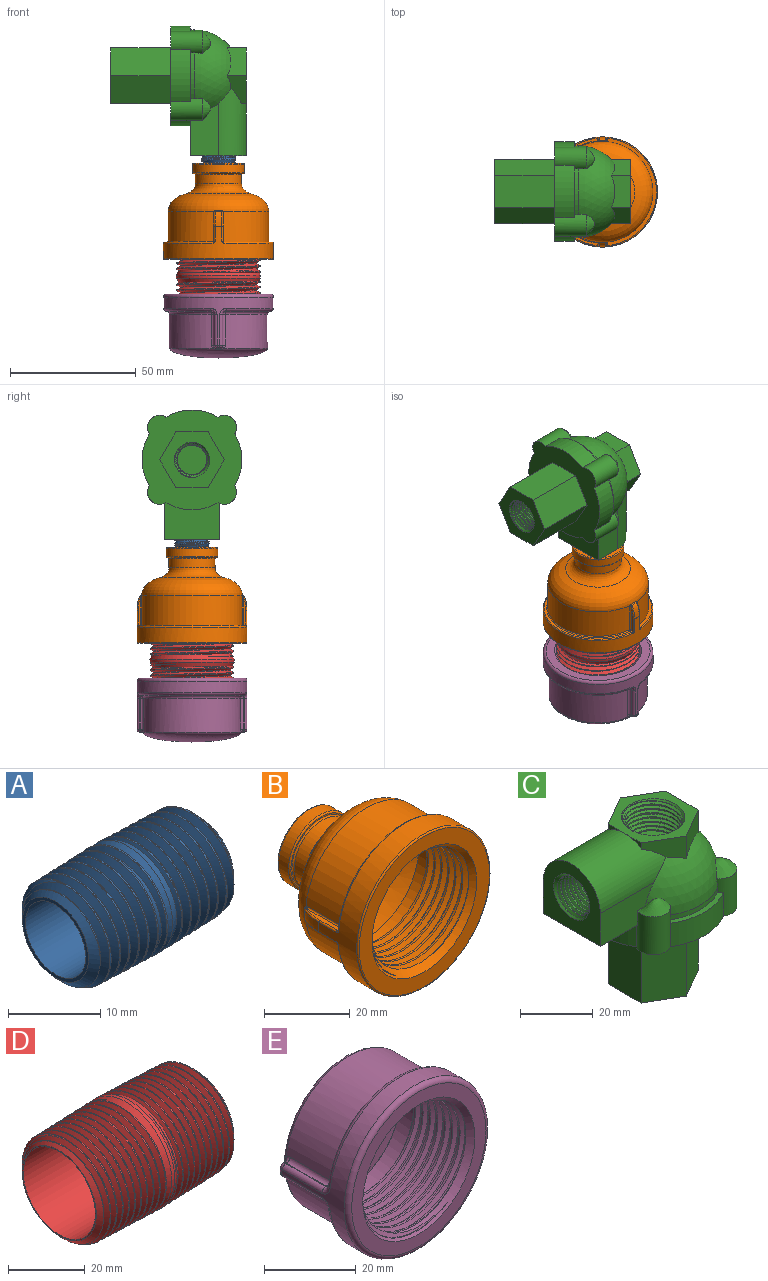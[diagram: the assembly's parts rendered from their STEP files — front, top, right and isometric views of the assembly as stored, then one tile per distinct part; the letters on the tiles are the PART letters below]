
ASSEMBLY  parts=5 mates=9
PART A: 109 faces, bbox 22.5x14.3x14.3 mm
  f0: plane 10.13x10.13mm, normal (-1,0,0), area 13.5mm2, adj f1,f108
  f1: cylinder r=4.62mm len=22.23mm, axis (1,0,0), area 645.5mm2, adj f0,f2
  f2: plane 10.13x10.13mm, normal (1,0,0), area 13.5mm2, adj f1,f3
  f3: cone r=5.07mm half-angle=46.8deg, axis (-1,0,0), area 44.8mm2, adj f2,f4,f106,f107
  f4: bspline ~12.19x12.15mm, area 38.6mm2, adj f3,f5,f105,f106
  f5: bspline ~13.46x13.4mm, area 266.1mm2, adj f4,f6,f7,f8,f9,f10,f11,f12
  f6: bspline ~3.82x0.92mm, area 0mm2, adj f5,f19,f107
  f7: bspline ~4.28x3.3mm, area 0mm2, adj f5,f19
  f8: bspline ~5.31x1.19mm, area 0mm2, adj f5,f19
  f9: bspline ~4.66x2.76mm, area 0mm2, adj f5,f19
  f10: bspline ~5.15x1.7mm, area 0mm2, adj f5,f19
  f11: bspline ~5.56x2.66mm, area 0mm2, adj f5,f19
  f12: bspline ~5.66x2.45mm, area 0mm2, adj f5,f19
  f13: bspline ~4.61x2.88mm, area 0mm2, adj f5,f19
  f14: bspline ~4.92x3.74mm, area 0mm2, adj f5,f19
  f15: bspline ~6.53x1.24mm, area 0mm2, adj f5,f19
  f16: bspline ~3.92x3.79mm, area 0mm2, adj f5,f19
  f17: bspline ~6.52x1.39mm, area 0mm2, adj f5,f19
  f18: bspline ~5.36x1.25mm, area 0mm2, adj f5,f19
  f19: cone r=6.86mm half-angle=1.8deg, axis (-1,0,0), area 71.4mm2, adj f5,f6,f7,f8,f9,f10,f11,f12
  f20: bspline ~6.23x2.37mm, area 0mm2, adj f5,f19
  f21: bspline ~6.05x2.65mm, area 0mm2, adj f5,f19
  f22: bspline ~4.95x2.37mm, area 0mm2, adj f5,f19
  f23: bspline ~5.28x1.57mm, area 0mm2, adj f5,f19
  f24: bspline ~5.15x3.53mm, area 0mm2, adj f5,f19
  f25: bspline ~5.44x1.08mm, area 0mm2, adj f5,f19
  f26: bspline ~5.08x4.22mm, area 0mm2, adj f5,f19
  f27: bspline ~6.25x1mm, area 0mm2, adj f5,f19
  f28: bspline ~4.82x4.54mm, area 0mm2, adj f5,f19
  f29: bspline ~5.5x0.86mm, area 0mm2, adj f5,f19
  f30: bspline ~4.46x3.27mm, area 0mm2, adj f5,f19
  f31: bspline ~5.41x1.32mm, area 0mm2, adj f5,f19
  f32: bspline ~5.79x3.25mm, area 0mm2, adj f5,f19
  f33: bspline ~5.99x2.15mm, area 0mm2, adj f5,f19
  f34: bspline ~5.14x2.1mm, area 0mm2, adj f5,f19
  f35: bspline ~5.97x2.97mm, area 0mm2, adj f5,f19
  f36: bspline ~6.03x2.18mm, area 0mm2, adj f5,f19
  f37: bspline ~4.65x3.06mm, area 0mm2, adj f5,f19
  f38: bspline ~5.51x1.05mm, area 0mm2, adj f5,f19
  f39: bspline ~4.24x3.61mm, area 0mm2, adj f5,f19
  f40: bspline ~6.68x1.16mm, area 0mm2, adj f5,f19
  f41: bspline ~4.11x3.78mm, area 0mm2, adj f5,f19
  f42: bspline ~6.32x1.29mm, area 0mm2, adj f5,f19
  f43: bspline ~4.55x3.25mm, area 0mm2, adj f5,f19
  f44: bspline ~5.45x1.38mm, area 0mm2, adj f5,f19
  f45: bspline ~4.92x2.68mm, area 0mm2, adj f5,f19
  f46: bspline ~6.31x2.52mm, area 0mm2, adj f5,f19
  f47: bspline ~5.58x2.31mm, area 0mm2, adj f5,f19
  f48: bspline ~5x2.55mm, area 0mm2, adj f5,f19
  f49: bspline ~5.44x1.5mm, area 0mm2, adj f5,f19
  f50: bspline ~4.98x2.91mm, area 0mm2, adj f5,f19,f51
  f51: cone r=6.52mm half-angle=45deg, axis (1,0,0), area 2.8mm2, adj f5,f19,f50,f52,f106
  f52: cone r=6.86mm half-angle=25deg, axis (-1,0,0), area 44.7mm2, adj f5,f51,f53,f105,f106
  f53: cone r=6.86mm half-angle=25deg, axis (1,0,0), area 43.3mm2, adj f52,f54,f56,f103,f104
  f54: cone r=6.86mm half-angle=25deg, axis (1,0,0), area 7.1mm2, adj f53,f55,f56,f104
  f55: bspline ~12.19x12.15mm, area 38.6mm2, adj f54,f56,f104,f108
  f56: bspline ~13.46x13.4mm, area 266.1mm2, adj f53,f54,f55,f57,f58,f59,f60,f61
  f57: cone r=5.07mm half-angle=46.8deg, axis (1,0,0), area 5.9mm2, adj f56,f58,f71,f104,f108
  f58: bspline ~3.82x0.92mm, area 0mm2, adj f56,f57,f71
  f59: bspline ~4.28x3.3mm, area 0mm2, adj f56,f71
  f60: bspline ~5.31x1.19mm, area 0mm2, adj f56,f71
  f61: bspline ~4.66x2.76mm, area 0mm2, adj f56,f71
  f62: bspline ~5.15x1.7mm, area 0mm2, adj f56,f71
  f63: bspline ~5.56x2.66mm, area 0mm2, adj f56,f71
  f64: bspline ~5.66x2.45mm, area 0mm2, adj f56,f71
  f65: bspline ~4.61x2.88mm, area 0mm2, adj f56,f71
  f66: bspline ~4.92x3.74mm, area 0mm2, adj f56,f71
  f67: bspline ~6.53x1.24mm, area 0mm2, adj f56,f71
  f68: bspline ~3.92x3.79mm, area 0mm2, adj f56,f71
  f69: bspline ~6.52x1.39mm, area 0mm2, adj f56,f71
  f70: bspline ~5.36x1.25mm, area 0mm2, adj f56,f71
  f71: cone r=6.86mm half-angle=1.8deg, axis (1,0,0), area 71.4mm2, adj f56,f57,f58,f59,f60,f61,f62,f63
  f72: bspline ~6.23x2.37mm, area 0mm2, adj f56,f71
  f73: bspline ~6.05x2.65mm, area 0mm2, adj f56,f71
  f74: bspline ~4.95x2.37mm, area 0mm2, adj f56,f71
  f75: bspline ~5.28x1.57mm, area 0mm2, adj f56,f71
  f76: bspline ~5.15x3.53mm, area 0mm2, adj f56,f71
  f77: bspline ~5.44x1.08mm, area 0mm2, adj f56,f71
  f78: bspline ~5.08x4.22mm, area 0mm2, adj f56,f71
  f79: bspline ~6.25x1mm, area 0mm2, adj f56,f71
  f80: bspline ~4.82x4.54mm, area 0mm2, adj f56,f71
  f81: bspline ~5.5x0.86mm, area 0mm2, adj f56,f71
  f82: bspline ~4.46x3.27mm, area 0mm2, adj f56,f71
  f83: bspline ~5.41x1.32mm, area 0mm2, adj f56,f71
  f84: bspline ~5.79x3.25mm, area 0mm2, adj f56,f71
  f85: bspline ~5.99x2.15mm, area 0mm2, adj f56,f71
  f86: bspline ~5.14x2.1mm, area 0mm2, adj f56,f71
  f87: bspline ~5.97x2.97mm, area 0mm2, adj f56,f71
  f88: bspline ~6.03x2.18mm, area 0mm2, adj f56,f71
  f89: bspline ~4.65x3.06mm, area 0mm2, adj f56,f71
  f90: bspline ~5.51x1.05mm, area 0mm2, adj f56,f71
  f91: bspline ~4.24x3.61mm, area 0mm2, adj f56,f71
  f92: bspline ~6.68x1.16mm, area 0mm2, adj f56,f71
  f93: bspline ~4.11x3.78mm, area 0mm2, adj f56,f71
  f94: bspline ~6.32x1.29mm, area 0mm2, adj f56,f71
  f95: bspline ~4.55x3.25mm, area 0mm2, adj f56,f71
  f96: bspline ~5.45x1.38mm, area 0mm2, adj f56,f71
  f97: bspline ~4.92x2.68mm, area 0mm2, adj f56,f71
  f98: bspline ~6.31x2.52mm, area 0mm2, adj f56,f71
  f99: bspline ~5.58x2.31mm, area 0mm2, adj f56,f71
  f100: bspline ~5x2.55mm, area 0mm2, adj f56,f71
  f101: bspline ~5.44x1.5mm, area 0mm2, adj f56,f71
  f102: bspline ~4.98x2.91mm, area 0mm2, adj f56,f71,f103
  f103: cone r=6.52mm half-angle=45deg, axis (-1,0,0), area 2.8mm2, adj f53,f56,f71,f102,f104
  f104: bspline ~14.26x14.19mm, area 271.6mm2, adj f53,f54,f55,f57,f71,f103,f108
  f105: cone r=6.86mm half-angle=25deg, axis (-1,0,0), area 5.6mm2, adj f4,f5,f52,f106
  f106: bspline ~14.26x14.19mm, area 269.3mm2, adj f3,f4,f19,f51,f52,f105,f107
  f107: cone r=5.07mm half-angle=46.8deg, axis (-1,0,0), area 5.9mm2, adj f3,f5,f6,f19,f106
  f108: cone r=5.07mm half-angle=46.8deg, axis (1,0,0), area 44.8mm2, adj f0,f55,f57,f104
PART B: 72 faces, bbox 47.9x38.9x47.9 mm
  f0: cylinder r=21.84mm len=43.69mm, axis (0,-1,0), area 868.5mm2, adj f32,f33,f34,f36,f37,f39,f41,f49
  f1: plane 11.17x1.12mm, normal (0,0,-1), area 10.8mm2, adj f38,f40,f41,f43
  f2: plane 11.17x1.12mm, normal (0,0,1), area 10.8mm2, adj f50,f51,f57,f58
  f3: plane 11.17x1.12mm, normal (0,0,1), area 10.8mm2, adj f63,f67,f68,f69
  f4: plane 11.17x1.12mm, normal (0,0,-1), area 10.8mm2, adj f46,f48,f53,f56
  f5: cylinder r=7.11mm len=14.22mm, axis (0,1,0), area 217mm2, adj f29,f35
  f6: cylinder r=20mm len=39.82mm, axis (0,-1,0), area 692.4mm2, adj f18,f55,f58,f62,f63,f64
  f7: cylinder r=20mm len=39.82mm, axis (0,-1,0), area 715.6mm2, adj f9,f18,f38,f40,f42,f46,f48,f52
  f8: plane 42.69x19.34mm, normal (0,1,0), area 64.4mm2, adj f33,f57,f62,f68
  f9: plane 42.69x19.34mm, normal (0,1,0), area 87.9mm2, adj f7,f32,f38,f46
  f10: plane 42.89x42.89mm, normal (0,-1,0), area 510mm2, adj f11,f34
  f11: cone r=17.25mm half-angle=45deg, axis (0,-1,0), area 182mm2, adj f10,f12,f13,f14,f15
  f12: bspline ~33.55x33.52mm, area 845.3mm2, adj f11,f13,f15,f16
  f13: bspline ~30.92x30.89mm, area 310.9mm2, adj f11,f12,f14,f16
  f14: bspline ~33.57x33.54mm, area 804.5mm2, adj f11,f13,f15,f16
  f15: cone r=16.7mm half-angle=1.8deg, axis (0,-1,0), area 205.5mm2, adj f11,f12,f14,f16
  f16: plane 34.99x34.99mm, normal (0,1,0), area 165.6mm2, adj f12,f13,f14,f15,f17
  f17: cylinder r=17.21mm len=34.42mm, axis (0,-1,0), area 466.9mm2, adj f16,f35
  f18: revolved ~40.01x40.01mm, area 1167.6mm2, adj f6,f7,f19,f44,f45,f47,f59,f61
  f19: revolved ~25.71x25.71mm, area 382.1mm2, adj f18,f20
  f20: cylinder r=9.14mm len=18.29mm, axis (0,1,0), area 211.4mm2, adj f19,f71
  f21: plane 19.78x19.78mm, normal (0,-1,0), area 21.3mm2, adj f31,f71
  f22: cylinder r=10.29mm len=20.57mm, axis (0,1,0), area 211.4mm2, adj f30,f31
  f23: plane 19.78x19.78mm, normal (0,1,0), area 143.9mm2, adj f24,f30
  f24: cone r=7.21mm half-angle=45deg, axis (0,1,0), area 47.5mm2, adj f23,f25,f26,f27,f28
  f25: bspline ~12.22x12.15mm, area 65.6mm2, adj f24,f26,f27,f29
  f26: bspline ~13.91x13.83mm, area 184.1mm2, adj f24,f25,f28,f29
  f27: bspline ~13.89x13.88mm, area 175.3mm2, adj f24,f25,f28,f29
  f28: cone r=6.86mm half-angle=1.8deg, axis (0,1,0), area 46.6mm2, adj f24,f26,f27,f29
  f29: plane 14.65x14.65mm, normal (0,-1,0), area 38.2mm2, adj f5,f25,f26,f27,f28
  f30: torus R=9.89mm, axis (0,-1,0), area 39.7mm2, adj f22,f23
  f31: torus R=9.89mm, axis (0,1,0), area 39.7mm2, adj f21,f22
  f32: torus R=21.45mm, axis (0,-1,0), area 39.8mm2, adj f0,f9,f39,f49
  f33: torus R=21.45mm, axis (0,-1,0), area 39.8mm2, adj f0,f8,f54,f70
  f34: torus R=21.45mm, axis (0,-1,0), area 85mm2, adj f0,f10
  f35: cone r=0mm half-angle=59deg, axis (0,-1,0), area 900mm2, adj f5,f17
  f36: revolved ~6.05x2.87mm, area 17.5mm2, adj f0,f43,f45,f51
  f37: revolved ~6.05x2.87mm, area 17.3mm2, adj f0,f56,f61,f67
  f38: cylinder r=0.4mm len=1.52mm, axis (-1,0,0), area 0.8mm2, adj f1,f7,f9,f39,f40
  f39: bspline ~0.97x0.95mm, area 0.5mm2, adj f0,f32,f38,f41
  f40: cylinder r=0.4mm len=11.56mm, axis (0,-1,0), area 6.6mm2, adj f1,f7,f38,f42
  f41: cylinder r=0.4mm len=5.7mm, axis (0,-1,0), area 3.4mm2, adj f0,f1,f39,f43
  f42: bspline ~1.11x0.5mm, area 0.3mm2, adj f7,f40,f43,f44
  f43: bspline ~7.42x1.8mm, area 3.7mm2, adj f1,f36,f41,f42,f44
  f44: bspline ~0.79x0.55mm, area 0.2mm2, adj f18,f42,f43,f45
  f45: torus R=20.39mm, axis (0,-1,0), area 1.2mm2, adj f18,f36,f44,f47
  f46: cylinder r=0.4mm len=1.52mm, axis (-1,0,0), area 0.8mm2, adj f4,f7,f9,f48,f49
  f47: bspline ~0.79x0.55mm, area 0.2mm2, adj f18,f45,f51,f55
  f48: cylinder r=0.4mm len=11.56mm, axis (0,-1,0), area 6.6mm2, adj f4,f7,f46,f52
  f49: bspline ~0.99x0.89mm, area 0.5mm2, adj f0,f32,f46,f53
  f50: cylinder r=0.4mm len=5.7mm, axis (0,-1,0), area 3.4mm2, adj f0,f2,f51,f54
  f51: bspline ~7.42x1.8mm, area 3.7mm2, adj f2,f36,f47,f50,f55
  f52: bspline ~1.11x0.5mm, area 0.3mm2, adj f7,f48,f56,f59
  f53: cylinder r=0.4mm len=5.7mm, axis (0,-1,0), area 3.4mm2, adj f0,f4,f49,f56
  f54: bspline ~0.99x0.89mm, area 0.5mm2, adj f0,f33,f50,f57
  f55: bspline ~1.11x0.5mm, area 0.3mm2, adj f6,f47,f51,f58
  f56: bspline ~7.42x1.8mm, area 3.7mm2, adj f4,f37,f52,f53,f59
  f57: cylinder r=0.4mm len=1.12mm, axis (1,0,0), area 0.7mm2, adj f2,f8,f54,f60
  f58: cylinder r=0.4mm len=11.17mm, axis (0,-1,0), area 6.5mm2, adj f2,f6,f55,f60
  f59: bspline ~0.79x0.55mm, area 0.2mm2, adj f18,f52,f56,f61
  f60: sphere r=0.4mm, area 0.3mm2, adj f57,f58,f62
  f61: torus R=20.39mm, axis (0,-1,0), area 1.2mm2, adj f18,f37,f59,f65
  f62: torus R=20.4mm, axis (0,-1,0), area 36.9mm2, adj f6,f8,f60,f66
  f63: cylinder r=0.4mm len=11.17mm, axis (0,-1,0), area 6.5mm2, adj f3,f6,f64,f66
  f64: bspline ~1.11x0.5mm, area 0.3mm2, adj f6,f63,f65,f67
  f65: bspline ~0.79x0.55mm, area 0.2mm2, adj f18,f61,f64,f67
  f66: sphere r=0.4mm, area 0.3mm2, adj f62,f63,f68
  f67: bspline ~7.42x1.8mm, area 3.7mm2, adj f3,f37,f64,f65,f69
  f68: cylinder r=0.4mm len=1.12mm, axis (1,0,0), area 0.7mm2, adj f3,f8,f66,f70
  f69: cylinder r=0.4mm len=5.7mm, axis (0,-1,0), area 3.4mm2, adj f0,f3,f67,f70
  f70: bspline ~0.97x0.95mm, area 0.5mm2, adj f0,f33,f68,f69
  f71: torus R=9.54mm, axis (0,1,0), area 36.4mm2, adj f20,f21
PART C: 58 faces, bbox 52.9x40.7x55.6 mm
  f0: plane 22.23x22.23mm, normal (-1,0,0), area 285.5mm2, adj f10,f11,f23,f29,f46
  f1: plane 25.66x22.23mm, normal (0,0,-1), area 272.3mm2, adj f14,f15,f16,f17,f18,f19,f40
  f2: plane 20.71x4.04mm, normal (0,0,1), area 32.3mm2, adj f4,f7,f33,f35
  f3: cylinder r=18.26mm len=18.26mm, axis (0,0,-1), area 30.4mm2, adj f6,f32,f35,f39
  f4: cylinder r=19.84mm len=20.71mm, axis (0,0,1), area 172.9mm2, adj f2,f13,f33,f35
  f5: cylinder r=19.84mm len=20.71mm, axis (0,0,1), area 172.9mm2, adj f9,f13,f31,f33
  f6: plane 20.71x4.04mm, normal (0,0,1), area 32.3mm2, adj f3,f8,f32,f35
  f7: cylinder r=18.26mm len=18.26mm, axis (0,0,-1), area 30.4mm2, adj f2,f33,f35,f39
  f8: cylinder r=19.84mm len=20.71mm, axis (0,0,1), area 172.9mm2, adj f6,f13,f32,f35
  f9: plane 20.71x4.04mm, normal (0,0,1), area 32.3mm2, adj f5,f30,f31,f33
  f10: plane 21.55x11.82mm, normal (0,-1,0), area 188.7mm2, adj f0,f23,f29,f32,f38,f39
  f11: plane 21.55x11.82mm, normal (0,1,0), area 188.7mm2, adj f0,f23,f29,f31,f37,f39
  f12: cylinder r=19.84mm len=20.71mm, axis (0,0,1), area 172.9mm2, adj f13,f29,f31,f32
  f13: plane 39.69x39.69mm, normal (0,0,-1), area 899mm2, adj f4,f5,f8,f12,f14,f15,f16,f17
  f14: plane 23.81x11.11mm, normal (-0.5,0.87,0), area 305.6mm2, adj f1,f13,f15,f19
  f15: plane 23.81x12.83mm, normal (-1,0,0), area 305.6mm2, adj f1,f13,f14,f16
  f16: plane 23.81x11.11mm, normal (-0.5,-0.87,0), area 305.6mm2, adj f1,f13,f15,f17
  f17: plane 23.81x11.11mm, normal (0.5,-0.87,0), area 305.6mm2, adj f1,f13,f16,f18
  f18: plane 23.81x12.83mm, normal (1,0,0), area 305.6mm2, adj f1,f13,f17,f19
  f19: plane 23.81x11.11mm, normal (0.5,0.87,0), area 305.6mm2, adj f1,f13,f14,f18
  f20: plane 6.42x2.04mm, normal (-1,0,0), area 4.2mm2, adj f21,f23,f24
  f21: plane 25.66x22.23mm, normal (0,0,1), area 187.3mm2, adj f20,f22,f24,f25,f26,f27,f28,f52
  f22: plane 6.42x2.04mm, normal (-1,0,0), area 4.2mm2, adj f21,f23,f27
  f23: cylinder r=11.11mm len=26.76mm, axis (1,0,0), area 786.5mm2, adj f0,f10,f11,f20,f22,f24,f27,f39
  f24: plane 12x8.54mm, normal (-0.5,-0.87,0), area 65.1mm2, adj f20,f21,f23,f25,f39
  f25: plane 11.11x7.65mm, normal (0.5,-0.87,0), area 85.2mm2, adj f21,f24,f26,f39
  f26: plane 12.83x7.65mm, normal (1,0,0), area 85.2mm2, adj f21,f25,f28,f39
  f27: plane 12.11x8.65mm, normal (-0.5,0.87,0), area 65.1mm2, adj f21,f22,f23,f28,f39
  f28: plane 11.11x7.65mm, normal (0.5,0.87,0), area 85.2mm2, adj f21,f26,f27,f39
  f29: plane 22.23x14.82mm, normal (0,0,-1), area 288.2mm2, adj f0,f10,f11,f12,f31,f32
  f30: cylinder r=18.26mm len=18.26mm, axis (0,0,-1), area 30.4mm2, adj f9,f31,f33,f39
  f31: cylinder r=4.76mm len=12.7mm, axis (0,0,-1), area 167.8mm2, adj f5,f9,f11,f12,f13,f29,f30,f37
  f32: cylinder r=4.76mm len=12.7mm, axis (0,0,-1), area 167.8mm2, adj f3,f6,f8,f10,f12,f13,f29,f38
  f33: cylinder r=4.76mm len=12.7mm, axis (0,0,-1), area 180.3mm2, adj f2,f4,f5,f7,f9,f13,f30,f34
  f34: bspline ~9.75x9.43mm, area 57.4mm2, adj f33,f39
  f35: cylinder r=4.76mm len=12.7mm, axis (0,0,-1), area 180.3mm2, adj f2,f3,f4,f6,f7,f8,f13,f36
  f36: bspline ~9.75x9.44mm, area 57.1mm2, adj f35,f39
  f37: bspline ~9.44x6.76mm, area 52.3mm2, adj f11,f31,f39
  f38: bspline ~9.43x6.76mm, area 52.4mm2, adj f10,f32,f39
  f39: sphere r=18.26mm, area 1046.6mm2, adj f3,f7,f10,f11,f23,f24,f25,f26
  f40: cone r=7.03mm half-angle=45deg, axis (0,0,-1), area 36mm2, adj f1,f42,f43,f44,f45
  f41: plane 12.69x12.55mm, normal (0,0,-1), area 118.2mm2, adj f42,f43,f44,f45
  f42: bspline ~12.34x12.3mm, area 100.6mm2, adj f40,f41,f43,f44
  f43: bspline ~13.98x13.93mm, area 230.1mm2, adj f40,f41,f42,f45
  f44: bspline ~13.96x13.91mm, area 218.4mm2, adj f40,f41,f42,f45
  f45: cone r=6.86mm half-angle=1.8deg, axis (0,0,-1), area 52.8mm2, adj f40,f41,f43,f44
  f46: cone r=7.03mm half-angle=45deg, axis (-1,0,0), area 36mm2, adj f0,f48,f49,f50,f51
  f47: plane 12.69x12.55mm, normal (-1,0,0), area 118.2mm2, adj f48,f49,f50,f51
  f48: bspline ~12.34x12.3mm, area 100.6mm2, adj f46,f47,f49,f50
  f49: bspline ~13.98x13.93mm, area 230.1mm2, adj f46,f47,f48,f51
  f50: bspline ~13.96x13.91mm, area 218.4mm2, adj f46,f47,f48,f51
  f51: cone r=6.86mm half-angle=1.8deg, axis (-1,0,0), area 52.8mm2, adj f46,f47,f49,f50
  f52: cone r=8.75mm half-angle=45deg, axis (0,0,1), area 45.3mm2, adj f21,f54,f55,f56,f57
  f53: plane 16.12x15.95mm, normal (0,0,1), area 193.2mm2, adj f54,f55,f56,f57
  f54: bspline ~15.81x15.75mm, area 131.6mm2, adj f52,f53,f55,f56
  f55: bspline ~17.45x17.38mm, area 296.8mm2, adj f52,f53,f54,f57
  f56: bspline ~17.43x17.36mm, area 281.8mm2, adj f52,f53,f54,f57
  f57: cone r=8.57mm half-angle=1.8deg, axis (0,0,1), area 68.6mm2, adj f52,f53,f55,f56
PART D: 22 faces, bbox 50.9x33.4x33.4 mm
  f0: plane 27.33x27.33mm, normal (-1,0,0), area 28.9mm2, adj f6,f11
  f1: bspline ~33.44x33.4mm, area 1522.5mm2, adj f3,f4,f5,f6,f7,f9
  f2: bspline ~33.36x33.33mm, area 1586.2mm2, adj f3,f4,f5,f7,f8,f9
  f3: bspline ~30.4x30.36mm, area 243.4mm2, adj f1,f2,f6,f8,f9
  f4: cone r=15.87mm half-angle=45deg, axis (-1,0,0), area 15.3mm2, adj f1,f2,f5,f9
  f5: cone r=16.7mm half-angle=1.8deg, axis (1,0,0), area 262.8mm2, adj f1,f2,f4,f7
  f6: cone r=13.66mm half-angle=46.8deg, axis (1,0,0), area 183mm2, adj f0,f1,f3,f7
  f7: cone r=13.66mm half-angle=46.8deg, axis (1,0,0), area 22.5mm2, adj f1,f2,f5,f6
  f8: cone r=16.7mm half-angle=25deg, axis (1,0,0), area 0.8mm2, adj f2,f3,f9
  f9: cone r=16.7mm half-angle=25deg, axis (1,0,0), area 201mm2, adj f1,f2,f3,f4,f8,f10
  f10: cylinder r=16.7mm len=33.4mm, axis (-1,0,0), area 115.9mm2, adj f9,f21
  f11: cylinder r=13.32mm len=50.8mm, axis (1,0,0), area 4252.3mm2, adj f0,f12
  f12: plane 27.33x27.33mm, normal (1,0,0), area 28.9mm2, adj f11,f18
  f13: bspline ~33.44x33.4mm, area 1522.5mm2, adj f15,f16,f17,f18,f19,f21
  f14: bspline ~33.36x33.33mm, area 1586.2mm2, adj f15,f16,f17,f19,f20,f21
  f15: bspline ~30.4x30.36mm, area 243.4mm2, adj f13,f14,f18,f20,f21
  f16: cone r=15.87mm half-angle=45deg, axis (1,0,0), area 15.3mm2, adj f13,f14,f17,f21
  f17: cone r=16.7mm half-angle=1.8deg, axis (-1,0,0), area 262.8mm2, adj f13,f14,f16,f19
  f18: cone r=13.66mm half-angle=46.8deg, axis (-1,0,0), area 183mm2, adj f12,f13,f15,f19
  f19: cone r=13.66mm half-angle=46.8deg, axis (-1,0,0), area 22.5mm2, adj f13,f14,f17,f18
  f20: cone r=16.7mm half-angle=25deg, axis (-1,0,0), area 0.8mm2, adj f14,f15,f21
  f21: cone r=16.7mm half-angle=25deg, axis (-1,0,0), area 201mm2, adj f10,f13,f14,f15,f16,f20
PART E: 65 faces, bbox 47.4x25.5x47.4 mm
  f0: cylinder r=19.49mm len=38.69mm, axis (0,-1,0), area 750.4mm2, adj f20,f45,f49,f54,f58,f59
  f1: cylinder r=19.49mm len=38.69mm, axis (0,-1,0), area 750.4mm2, adj f20,f21,f25,f27,f34,f38
  f2: plane 41.34x41.34mm, normal (0,-1,0), area 407mm2, adj f4,f5
  f3: cylinder r=21.84mm len=43.69mm, axis (0,-1,0), area 657.2mm2, adj f4,f26,f31,f32,f37,f41,f42,f51
  f4: torus R=20.67mm, axis (0,-1,0), area 248.3mm2, adj f2,f3
  f5: cone r=17.25mm half-angle=45deg, axis (0,-1,0), area 154.5mm2, adj f2,f7,f8,f9,f10
  f6: plane 28.06x27.47mm, normal (0,-1,0), area 18.4mm2, adj f7,f9,f10,f16
  f7: bspline ~33.59x33.53mm, area 816.3mm2, adj f5,f6,f8,f10,f15
  f8: bspline ~31.47x31.41mm, area 384.4mm2, adj f5,f7,f9,f15
  f9: bspline ~33.6x33.57mm, area 773.5mm2, adj f5,f6,f8,f10,f15
  f10: cone r=16.7mm half-angle=1.8deg, axis (0,-1,0), area 458.2mm2, adj f5,f6,f7,f9
  f11: plane 12.27x0.2mm, normal (0,0,-1), area 2.4mm2, adj f33,f34,f42,f43
  f12: plane 12.27x0.2mm, normal (0,0,1), area 2.4mm2, adj f53,f58,f61,f64
  f13: plane 12.27x0.2mm, normal (0,0,1), area 2.4mm2, adj f40,f49,f50,f51
  f14: plane 12.27x0.2mm, normal (0,0,-1), area 2.4mm2, adj f21,f22,f30,f31
  f15: plane 26.78x26.15mm, normal (0,1,0), area 16.3mm2, adj f7,f8,f9,f16
  f16: cylinder r=15.68mm len=31.37mm, axis (0,-1,0), area 407.8mm2, adj f6,f15,f17
  f17: revolved ~31.37x15.68mm, area 0mm2, adj f16
  f18: plane 1.08x0.38mm, normal (0,1,0), area 0.4mm2, adj f43,f44,f52,f53
  f19: plane 1.08x0.38mm, normal (0,1,0), area 0.4mm2, adj f29,f30,f40,f41
  f20: revolved ~38.99x38.99mm, area 1302.5mm2, adj f0,f1,f24,f29,f35,f39,f44,f48
  f21: cylinder r=1.17mm len=12.27mm, axis (0,-1,0), area 20.6mm2, adj f1,f14,f23,f25
  f22: cylinder r=1.17mm len=1.17mm, axis (-1,0,0), area 0.2mm2, adj f14,f23,f26
  f23: sphere r=1.17mm, area 2mm2, adj f21,f22,f27
  f24: bspline ~2.47x1.21mm, area 2mm2, adj f20,f25,f29,f30
  f25: bspline ~1.98x1.31mm, area 1.4mm2, adj f1,f21,f24,f30
  f26: bspline ~2.75x2.63mm, area 4.7mm2, adj f3,f22,f31,f32
  f27: torus R=20.67mm, axis (0,-1,0), area 105.2mm2, adj f1,f23,f28,f32
  f28: sphere r=1.17mm, area 2mm2, adj f27,f33,f34
  f29: torus R=20.3mm, axis (0,-1,0), area 1.2mm2, adj f19,f20,f24,f35
  f30: cylinder r=1.17mm len=1.17mm, axis (1,0,0), area 0.4mm2, adj f14,f19,f24,f25,f36
  f31: cylinder r=1.17mm len=12.27mm, axis (0,-1,0), area 22.3mm2, adj f3,f14,f26,f36
  f32: torus R=20.67mm, axis (0,-1,0), area 113.1mm2, adj f3,f26,f27,f37
  f33: cylinder r=1.17mm len=1.17mm, axis (-1,0,0), area 0.2mm2, adj f11,f28,f37
  f34: cylinder r=1.17mm len=12.27mm, axis (0,-1,0), area 20.6mm2, adj f1,f11,f28,f38
  f35: bspline ~2.13x1.21mm, area 2mm2, adj f20,f29,f40,f45
  f36: sphere r=1.17mm, area 2.1mm2, adj f30,f31,f41
  f37: bspline ~2.89x2.88mm, area 4.7mm2, adj f3,f32,f33,f42
  f38: bspline ~1.98x1.31mm, area 1.4mm2, adj f1,f34,f39,f43
  f39: bspline ~2.13x1.21mm, area 2mm2, adj f20,f38,f43,f44
  f40: cylinder r=1.17mm len=1.17mm, axis (-1,0,0), area 0.4mm2, adj f13,f19,f35,f45,f46
  f41: torus R=20.67mm, axis (0,-1,0), area 2.1mm2, adj f3,f19,f36,f46
  f42: cylinder r=1.17mm len=12.27mm, axis (0,-1,0), area 22.3mm2, adj f3,f11,f37,f47
  f43: cylinder r=1.17mm len=1.17mm, axis (1,0,0), area 0.4mm2, adj f11,f18,f38,f39,f47
  f44: torus R=20.3mm, axis (0,-1,0), area 1.2mm2, adj f18,f20,f39,f48
  f45: bspline ~1.98x1.31mm, area 1.4mm2, adj f0,f35,f40,f49
  f46: sphere r=1.17mm, area 2.1mm2, adj f40,f41,f51
  f47: sphere r=1.17mm, area 2.1mm2, adj f42,f43,f52
  f48: bspline ~2.47x1.21mm, area 2mm2, adj f20,f44,f53,f54
  f49: cylinder r=1.17mm len=12.27mm, axis (0,-1,0), area 20.6mm2, adj f0,f13,f45,f55
  f50: cylinder r=1.17mm len=1.17mm, axis (1,0,0), area 0.2mm2, adj f13,f55,f56
  f51: cylinder r=1.17mm len=12.27mm, axis (0,-1,0), area 22.3mm2, adj f3,f13,f46,f56
  f52: torus R=20.67mm, axis (0,-1,0), area 2.1mm2, adj f3,f18,f47,f57
  f53: cylinder r=1.17mm len=1.17mm, axis (-1,0,0), area 0.4mm2, adj f12,f18,f48,f54,f57
  f54: bspline ~1.98x1.31mm, area 1.4mm2, adj f0,f48,f53,f58
  f55: sphere r=1.17mm, area 2mm2, adj f49,f50,f59
  f56: bspline ~2.89x2.88mm, area 4.7mm2, adj f3,f50,f51,f60
  f57: sphere r=1.17mm, area 2.1mm2, adj f52,f53,f61
  f58: cylinder r=1.17mm len=12.27mm, axis (0,-1,0), area 20.6mm2, adj f0,f12,f54,f62
  f59: torus R=20.67mm, axis (0,-1,0), area 105.2mm2, adj f0,f55,f60,f62
  f60: torus R=20.67mm, axis (0,-1,0), area 113.1mm2, adj f3,f56,f59,f63
  f61: cylinder r=1.17mm len=12.27mm, axis (0,-1,0), area 22.3mm2, adj f3,f12,f57,f63
  f62: sphere r=1.17mm, area 2mm2, adj f58,f59,f64
  f63: bspline ~3.05x2.75mm, area 4.7mm2, adj f3,f60,f61,f64
  f64: cylinder r=1.17mm len=1.17mm, axis (1,0,0), area 0.2mm2, adj f12,f62,f63
PLACE A rot(axis=(0,1,0),90deg) t=(-77.79,15.02,-18.3)mm
PLACE B rot(axis=(0.58,-0.58,-0.58),120deg) t=(-77.79,15.02,-38.87)mm
PLACE C rot(axis=(-0.71,0,-0.71),180deg) t=(-93.66,15.02,14.98)mm
PLACE D rot(axis=(0,-1,0),90deg) t=(-77.79,15.02,-64.82)mm
PLACE E rot(axis=(-0.58,0.58,-0.58),120deg) t=(-77.79,15.02,-97.13)mm
MATE planar D.f16 <-> B.f0  axis (0,0,1) through (-77.79,15.02,-64.27)mm
MATE parallel E.f13 <-> B.f4  axis (1,0,0) through (-76.07,-5.55,-85.9)mm
MATE slider B.f20 <-> A.f3  axis (0,0,1) through (-77.79,15.02,-19.82)mm
MATE slider E.f5 <-> D.f10  axis (0,0,1) through (-77.79,15.02,-71.73)mm
MATE planar A.f3 <-> B.f45  axis (0,0,-1) through (-77.79,15.02,-18.3)mm
MATE planar A.f3 <-> C.f23  axis (0,0,-1) through (-77.79,15.02,-18.3)mm
MATE planar D.f10 <-> E.f41  axis (0,0,-1) through (-77.79,15.02,-65.38)mm
MATE slider B.f5 <-> D.f10  axis (0,0,-1) through (-77.79,15.02,-57.92)mm
MATE slider A.f3 <-> C.f23  axis (0,0,-1) through (-77.79,15.02,-18.3)mm
